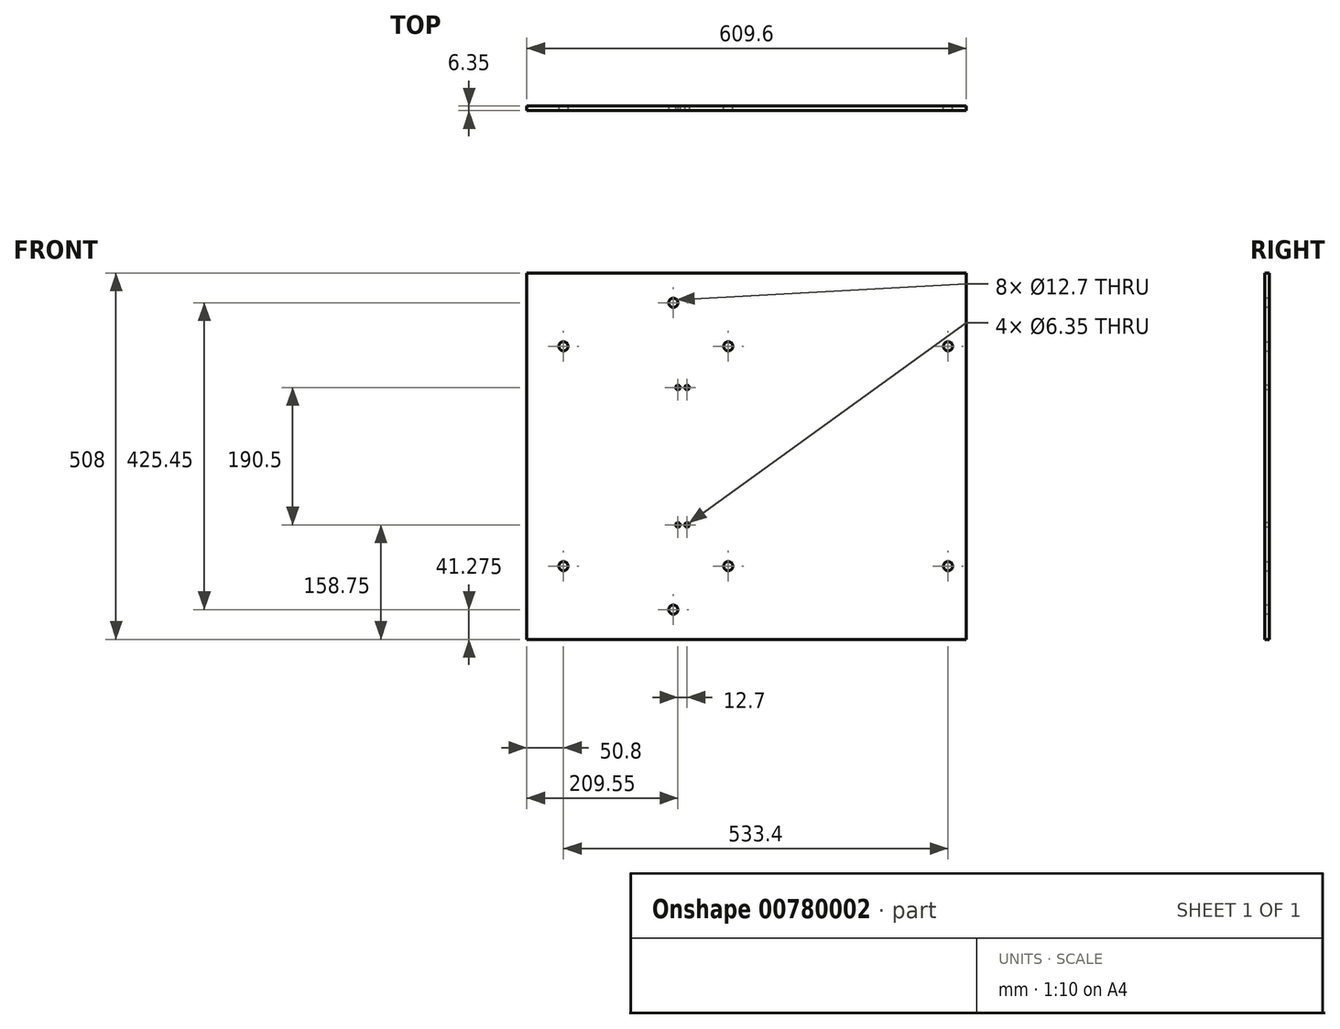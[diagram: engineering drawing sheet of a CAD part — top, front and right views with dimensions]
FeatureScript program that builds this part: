
annotation { "Feature Type Name" : "Feature", "Feature Type Description" : "" }
export const myFeature = defineFeature(function(context is Context, id is Id, definition is map)
    precondition{}
    {
        {
            var Q0;
            Q0=qCreatedBy(makeId("Front.planeOp"),FACE);
            var sketch = newSketch(context, id + "F0", { "sketchPlane" : qUnion([Q0])});
            skLineSegment(sketch, "E0.bottom", {"start": v(0, 0) * mm, "end": v(609.6, 0) * mm});
            skLineSegment(sketch, "E0.top", {"start": v(0, 508) * mm, "end": v(609.6, 508) * mm});
            skLineSegment(sketch, "E0.left", {"start": v(0, 0) * mm, "end": v(0, 508) * mm});
            skLineSegment(sketch, "E0.right", {"start": v(609.6, 0) * mm, "end": v(609.6, 508) * mm});
            skCircle(sketch, "E1", {"center": v(584.2, 101.6) * mm, "radius": 6.35 * mm});
            skCircle(sketch, "E2", {"center": v(279.4, 101.6) * mm, "radius": 6.35 * mm});
            skCircle(sketch, "E3", {"center": v(584.2, 406.4) * mm, "radius": 6.35 * mm});
            skCircle(sketch, "E4", {"center": v(279.4, 406.4) * mm, "radius": 6.35 * mm});
            skSolve(sketch);
        }
        {
            var Q0;
            Q0 = qSketchRegion(id + "F0", true);
            extrude(context, id + "F1", {"entities" : qUnion([Q0]), "depth" : 6.35 * mm, "offsetDistance" : 25.4 * mm});
        }
        {
            var Q0;
            Q0=makeQuery(id+"F1.opExtrude","CAP_FACE",FACE,{"disambiguationData":[OSD([sQuery(id+"F0.wireOp",EDGE,"E0.bottom"),sQuery(id+"F0.wireOp",EDGE,"E0.top"),sQuery(id+"F0.wireOp",EDGE,"E0.left"),sQuery(id+"F0.wireOp",EDGE,"E0.right"),sQuery(id+"F0.wireOp",EDGE,"E1"),sQuery(id+"F0.wireOp",EDGE,"E2"),sQuery(id+"F0.wireOp",EDGE,"E3"),sQuery(id+"F0.wireOp",EDGE,"E4")])],"isStart":false});
            var sketch = newSketch(context, id + "F2", { "sketchPlane" : qUnion([Q0])});
            skLineSegment(sketch, "E5", {"start": v(0, 254) * mm, "end": v(609.6, 254) * mm, "construction": true});
            skCircle(sketch, "E6", {"center": v(209.55, 158.75) * mm, "radius": 3.17 * mm});
            skCircle(sketch, "E7", {"center": v(222.25, 158.75) * mm, "radius": 3.17 * mm});
            skCircle(sketch, "E8.MirrorC", {"center": v(209.55, 349.25) * mm, "radius": 3.17 * mm});
            skCircle(sketch, "E9.MirrorC", {"center": v(222.25, 349.25) * mm, "radius": 3.17 * mm});
            skSolve(sketch);
        }
        {
            var Q0;
            Q0 = qSketchRegion(id + "F2", true);
            extrude(context, id + "F3", {"entities" : qUnion([Q0]), "operationType" : NewBodyOperationType.REMOVE, "oppositeDirection" : true, "depth" : 25.4 * mm, "offsetDistance" : 25.4 * mm});
        }
        {
            var Q0;
            Q0=makeQuery(id+"F1.opExtrude","CAP_FACE",FACE,{"disambiguationData":[OSD([sQuery(id+"F0.wireOp",EDGE,"E0.bottom"),sQuery(id+"F0.wireOp",EDGE,"E0.top"),sQuery(id+"F0.wireOp",EDGE,"E0.left"),sQuery(id+"F0.wireOp",EDGE,"E0.right"),sQuery(id+"F0.wireOp",EDGE,"E1"),sQuery(id+"F0.wireOp",EDGE,"E2"),sQuery(id+"F0.wireOp",EDGE,"E3"),sQuery(id+"F0.wireOp",EDGE,"E4")])],"isStart":false});
            var sketch = newSketch(context, id + "F4", { "sketchPlane" : qUnion([Q0])});
            skLineSegment(sketch, "E10", {"start": v(50.8, 508) * mm, "end": v(50.8, 0) * mm, "construction": true});
            skLineSegment(sketch, "E11", {"start": v(0, 254) * mm, "end": v(609.6, 254) * mm, "construction": true});
            skCircle(sketch, "E12", {"center": v(50.8, 406.4) * mm, "radius": 6.35 * mm});
            skCircle(sketch, "E13.MirrorC", {"center": v(50.8, 101.6) * mm, "radius": 6.35 * mm});
            skSolve(sketch);
        }
        {
            var Q0;
            Q0 = qSketchRegion(id + "F4", true);
            extrude(context, id + "F5", {"entities" : qUnion([Q0]), "operationType" : NewBodyOperationType.REMOVE, "oppositeDirection" : true, "depth" : 25.4 * mm, "offsetDistance" : 25.4 * mm});
        }
        {
            var Q0;
            Q0=makeQuery(id+"F1.opExtrude","CAP_FACE",FACE,{"disambiguationData":[OSD([sQuery(id+"F0.wireOp",EDGE,"E0.bottom"),sQuery(id+"F0.wireOp",EDGE,"E0.top"),sQuery(id+"F0.wireOp",EDGE,"E0.left"),sQuery(id+"F0.wireOp",EDGE,"E0.right"),sQuery(id+"F0.wireOp",EDGE,"E1"),sQuery(id+"F0.wireOp",EDGE,"E2"),sQuery(id+"F0.wireOp",EDGE,"E3"),sQuery(id+"F0.wireOp",EDGE,"E4")])],"isStart":false});
            var sketch = newSketch(context, id + "F6", { "sketchPlane" : qUnion([Q0])});
            skLineSegment(sketch, "E14", {"start": v(0, 254) * mm, "end": v(609.6, 254) * mm, "construction": true});
            skCircle(sketch, "E15", {"center": v(203.2, 41.28) * mm, "radius": 6.35 * mm});
            skCircle(sketch, "E16.MirrorC", {"center": v(203.2, 466.73) * mm, "radius": 6.35 * mm});
            skSolve(sketch);
        }
        {
            var Q0;
            Q0 = qSketchRegion(id + "F6", true);
            extrude(context, id + "F7", {"entities" : qUnion([Q0]), "operationType" : NewBodyOperationType.REMOVE, "oppositeDirection" : true, "depth" : 25.4 * mm, "offsetDistance" : 25.4 * mm});
        }
    });
